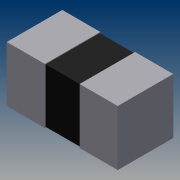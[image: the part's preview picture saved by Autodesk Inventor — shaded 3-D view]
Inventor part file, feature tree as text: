
AUTODESK INVENTOR PART (.ipt)
format: ipt  version: 2011 (Build 150239000, 239)  size: 112,640 bytes
history: native  units: mm
features: extrude x5, sketch x5, other x1
ambient origin geometry x8: Origin, YZ Plane, XZ Plane, XY Plane, X Axis, Y Axis, Z Axis, Center Point
feature tree (11):
  other  "Твердое тело1"
  extrude  "Выдавливание1"  Depth=1.6mm
  extrude  "Выдавливание2"  Depth=0.8mm
  extrude  "Выдавливание3"  Depth=0.8mm
  extrude  "Выдавливание4"  Depth=0.8mm
  extrude  "Выдавливание5"  Depth=0.4mm
  sketch  "Эскиз1"
  sketch  "Эскиз2"
  sketch  "Эскиз3"
  sketch  "Эскиз4"
  sketch  "Эскиз5"
